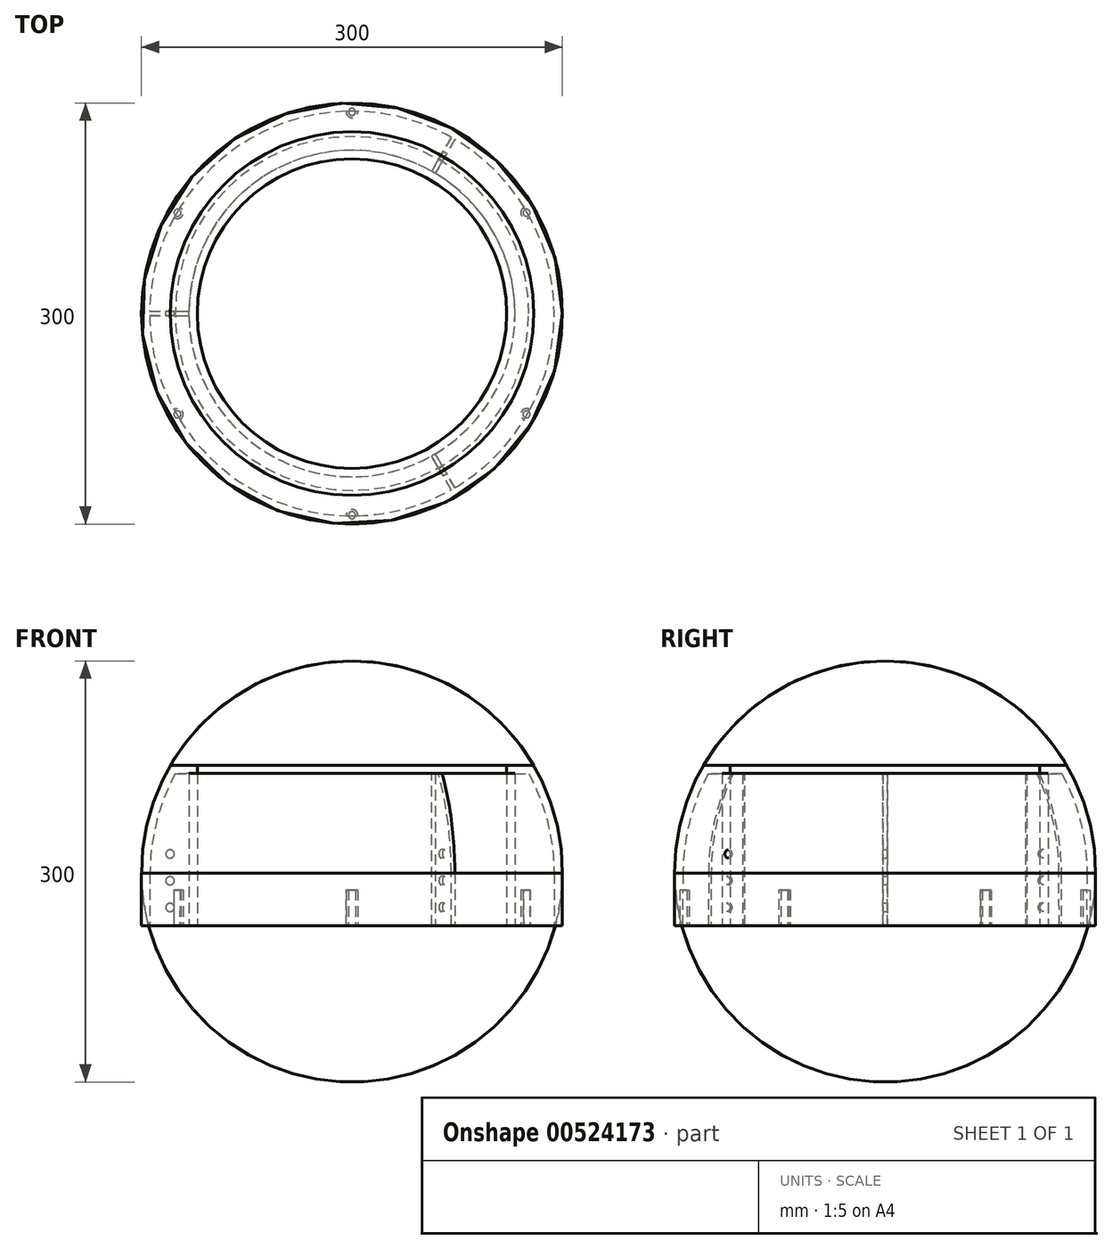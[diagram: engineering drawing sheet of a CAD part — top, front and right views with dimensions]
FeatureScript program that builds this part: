
annotation { "Feature Type Name" : "Feature", "Feature Type Description" : "" }
export const myFeature = defineFeature(function(context is Context, id is Id, definition is map)
    precondition{}
    {
        {
            var Q0;
            Q0=qCreatedBy(makeId("Front.planeOp"),FACE);
            var sketch = newSketch(context, id + "F0", { "sketchPlane" : qUnion([Q0])});
            skArc(sketch, "E0.trimOffspring", {"start": v(-125.97, 71) * mm, "mid": v(-139.35, 36.6) * mm, "end": v(-144, 0) * mm});
            skLineSegment(sketch, "E1", {"start": v(-116.3, 71.03) * mm, "end": v(-116.3, -24.99) * mm});
            skLineSegment(sketch, "E2", {"start": v(-150, 0) * mm, "end": v(-150, -37.33) * mm});
            skLineSegment(sketch, "E3", {"start": v(-150, -37.33) * mm, "end": v(-116.3, -37.33) * mm});
            skLineSegment(sketch, "E4", {"start": v(-116.3, -37.33) * mm, "end": v(-116.3, -24.99) * mm});
            skLineSegment(sketch, "E5", {"start": v(-144, 0) * mm, "end": v(-144.14, -37.33) * mm});
            skArc(sketch, "E6.trimOffspring", {"start": v(-129.51, 76.97) * mm, "mid": v(-144.96, 39.87) * mm, "end": v(-150, 0) * mm});
            skLineSegment(sketch, "E7", {"start": v(-129.51, 76.97) * mm, "end": v(-116.3, 76.97) * mm});
            skLineSegment(sketch, "E8", {"start": v(-116.3, 71.03) * mm, "end": v(-125.97, 71) * mm});
            skLineSegment(sketch, "E9", {"start": v(-125.99, 70.97) * mm, "end": v(-116.3, 70.97) * mm});
            skLineSegment(sketch, "E10", {"start": v(-110.3, 70.97) * mm, "end": v(-110.3, -37.33) * mm});
            skLineSegment(sketch, "E11", {"start": v(-110.3, -37.33) * mm, "end": v(-116.3, -37.33) * mm});
            skLineSegment(sketch, "E12", {"start": v(-116.3, 76.97) * mm, "end": v(-110.3, 76.97) * mm});
            skLineSegment(sketch, "E13", {"start": v(-110.3, 76.97) * mm, "end": v(-110.3, 70.97) * mm});
            skLineSegment(sketch, "E14", {"start": v(0, -70.43) * mm, "end": v(0, 79.54) * mm, "construction": true});
            skSolve(sketch);
        }
        {
            var Q0;
            {var subQ6=sQuery(id+"F0.wireOp",EDGE,"E2");Q0=makeQuery(id+"F0.imprint","IMPRINT",FACE,{"disambiguationData":[TD([[makeQuery(id+"F0.imprint","IMPRINT",EDGE,{"derivedFrom":subQ6}),1.0]])]});}
            var Q1;
            Q1=sQuery(id+"F0.wireOp",EDGE,"E14");
            revolve(context, id + "F1", {"entities" : qUnion([Q0]), "axis" : qUnion([Q1]), "revolveType" : RevolveType.FULL});
        }
        {
            var Q0;
            Q0=makeQuery(id+"F1.opRevolve","SWEPT_FACE",FACE,{"disambiguationData":[OSD([sQuery(id+"F0.wireOp",EDGE,"E3")])]});
            var sketch = newSketch(context, id + "F2", { "sketchPlane" : qUnion([Q0])});
            skCircle(sketch, "E15", {"center": v(0, 143.67) * mm, "radius": 2.5 * mm});
            skCircle(sketch, "E16", {"center": v(0, 143.67) * mm, "radius": 4.13 * mm});
            skCircle(sketch, "E17.1.0", {"center": v(-124.42, 71.83) * mm, "radius": 2.5 * mm});
            skCircle(sketch, "E17.2.0", {"center": v(-124.42, -71.83) * mm, "radius": 2.5 * mm});
            skCircle(sketch, "E17.3.0", {"center": v(0, -143.67) * mm, "radius": 2.5 * mm});
            skCircle(sketch, "E17.4.0", {"center": v(124.42, -71.83) * mm, "radius": 2.5 * mm});
            skCircle(sketch, "E17.5.0", {"center": v(124.42, 71.83) * mm, "radius": 2.5 * mm});
            skPoint(sketch, "E17.center", {"position": v(0, 0) * mm});
            skCircle(sketch, "E18.1.0", {"center": v(-124.42, -71.83) * mm, "radius": 4.13 * mm});
            skCircle(sketch, "E18.2.0", {"center": v(124.42, -71.83) * mm, "radius": 4.13 * mm});
            skCircle(sketch, "E19.1.0", {"center": v(-124.42, 71.83) * mm, "radius": 4.13 * mm});
            skCircle(sketch, "E19.3.0", {"center": v(0, -143.67) * mm, "radius": 4.13 * mm});
            skCircle(sketch, "E19.5.0", {"center": v(124.42, 71.83) * mm, "radius": 4.13 * mm});
            skSolve(sketch);
        }
        {
            var Q0;
            {var subQ0=sQuery(id+"F2.wireOp",EDGE,"E17.4.0");var subQ1=makeQuery(id+"F1.opRevolve","SWEPT_EDGE",EDGE,{"disambiguationData":[OSD([sQuery(id+"F0.wireOp",EDGE,"E3"),sQuery(id+"F0.wireOp",EDGE,"E5")])]});var subQ2=makeQuery(id+"F2.imprint","INTERSECT",VERTEX,{"disambiguationData":[OD(0.0)],"derivedFrom":[subQ1,subQ0]});Q0=makeQuery(id+"F2.imprint","IMPRINT",FACE,{"disambiguationData":[TD([[makeQuery(id+"F2.imprint","IMPRINT",EDGE,{"disambiguationData":[TD([[subQ2,-1.0]])],"derivedFrom":subQ0}),1.0]])]});}
            var Q1;
            {var subQ0=sQuery(id+"F2.wireOp",EDGE,"E15");var subQ1=makeQuery(id+"F1.opRevolve","SWEPT_EDGE",EDGE,{"disambiguationData":[OSD([sQuery(id+"F0.wireOp",EDGE,"E3"),sQuery(id+"F0.wireOp",EDGE,"E5")])]});var subQ2=makeQuery(id+"F2.imprint","INTERSECT",VERTEX,{"disambiguationData":[OD(0.0)],"derivedFrom":[subQ1,subQ0]});Q1=makeQuery(id+"F2.imprint","IMPRINT",FACE,{"disambiguationData":[TD([[makeQuery(id+"F2.imprint","IMPRINT",EDGE,{"disambiguationData":[TD([[subQ2,1.0]])],"derivedFrom":subQ0}),-1.0]])]});}
            var Q2;
            {var subQ0=sQuery(id+"F2.wireOp",EDGE,"E15");var subQ1=makeQuery(id+"F1.opRevolve","SWEPT_EDGE",EDGE,{"disambiguationData":[OSD([sQuery(id+"F0.wireOp",EDGE,"E3"),sQuery(id+"F0.wireOp",EDGE,"E5")])]});var subQ2=makeQuery(id+"F2.imprint","INTERSECT",VERTEX,{"disambiguationData":[OD(0.0)],"derivedFrom":[subQ1,subQ0]});Q2=makeQuery(id+"F2.imprint","IMPRINT",FACE,{"disambiguationData":[TD([[makeQuery(id+"F2.imprint","IMPRINT",EDGE,{"disambiguationData":[TD([[subQ2,-1.0]])],"derivedFrom":subQ0}),-1.0]])]});}
            var Q3;
            {var subQ0=sQuery(id+"F2.wireOp",EDGE,"E17.1.0");var subQ1=makeQuery(id+"F1.opRevolve","SWEPT_EDGE",EDGE,{"disambiguationData":[OSD([sQuery(id+"F0.wireOp",EDGE,"E3"),sQuery(id+"F0.wireOp",EDGE,"E5")])]});var subQ2=makeQuery(id+"F2.imprint","INTERSECT",VERTEX,{"disambiguationData":[OD(0.0)],"derivedFrom":[subQ1,subQ0]});Q3=makeQuery(id+"F2.imprint","IMPRINT",FACE,{"disambiguationData":[TD([[makeQuery(id+"F2.imprint","IMPRINT",EDGE,{"disambiguationData":[TD([[subQ2,-1.0]])],"derivedFrom":subQ0}),-1.0]])]});}
            var Q4;
            {var subQ0=sQuery(id+"F2.wireOp",EDGE,"E17.1.0");var subQ1=makeQuery(id+"F1.opRevolve","SWEPT_EDGE",EDGE,{"disambiguationData":[OSD([sQuery(id+"F0.wireOp",EDGE,"E3"),sQuery(id+"F0.wireOp",EDGE,"E5")])]});var subQ2=makeQuery(id+"F2.imprint","INTERSECT",VERTEX,{"disambiguationData":[OD(0.0)],"derivedFrom":[subQ1,subQ0]});Q4=makeQuery(id+"F2.imprint","IMPRINT",FACE,{"disambiguationData":[TD([[makeQuery(id+"F2.imprint","IMPRINT",EDGE,{"disambiguationData":[TD([[subQ2,1.0]])],"derivedFrom":subQ0}),-1.0]])]});}
            var Q5;
            {var subQ0=sQuery(id+"F2.wireOp",EDGE,"E17.5.0");var subQ1=makeQuery(id+"F1.opRevolve","SWEPT_EDGE",EDGE,{"disambiguationData":[OSD([sQuery(id+"F0.wireOp",EDGE,"E3"),sQuery(id+"F0.wireOp",EDGE,"E5")])]});var subQ2=makeQuery(id+"F2.imprint","INTERSECT",VERTEX,{"disambiguationData":[OD(0.0)],"derivedFrom":[subQ1,subQ0]});Q5=makeQuery(id+"F2.imprint","IMPRINT",FACE,{"disambiguationData":[TD([[makeQuery(id+"F2.imprint","IMPRINT",EDGE,{"disambiguationData":[TD([[subQ2,-1.0]])],"derivedFrom":subQ0}),-1.0]])]});}
            var Q6;
            {var subQ0=sQuery(id+"F2.wireOp",EDGE,"E17.5.0");var subQ1=makeQuery(id+"F1.opRevolve","SWEPT_EDGE",EDGE,{"disambiguationData":[OSD([sQuery(id+"F0.wireOp",EDGE,"E3"),sQuery(id+"F0.wireOp",EDGE,"E5")])]});var subQ2=makeQuery(id+"F2.imprint","INTERSECT",VERTEX,{"disambiguationData":[OD(0.0)],"derivedFrom":[subQ1,subQ0]});Q6=makeQuery(id+"F2.imprint","IMPRINT",FACE,{"disambiguationData":[TD([[makeQuery(id+"F2.imprint","IMPRINT",EDGE,{"disambiguationData":[TD([[subQ2,1.0]])],"derivedFrom":subQ0}),-1.0]])]});}
            var Q7;
            {var subQ0=sQuery(id+"F2.wireOp",EDGE,"E17.2.0");var subQ1=makeQuery(id+"F1.opRevolve","SWEPT_EDGE",EDGE,{"disambiguationData":[OSD([sQuery(id+"F0.wireOp",EDGE,"E3"),sQuery(id+"F0.wireOp",EDGE,"E5")])]});var subQ2=makeQuery(id+"F2.imprint","INTERSECT",VERTEX,{"disambiguationData":[OD(0.0)],"derivedFrom":[subQ1,subQ0]});Q7=makeQuery(id+"F2.imprint","IMPRINT",FACE,{"disambiguationData":[TD([[makeQuery(id+"F2.imprint","IMPRINT",EDGE,{"disambiguationData":[TD([[subQ2,-1.0]])],"derivedFrom":subQ0}),-1.0]])]});}
            var Q8;
            {var subQ0=sQuery(id+"F2.wireOp",EDGE,"E17.2.0");var subQ1=makeQuery(id+"F1.opRevolve","SWEPT_EDGE",EDGE,{"disambiguationData":[OSD([sQuery(id+"F0.wireOp",EDGE,"E3"),sQuery(id+"F0.wireOp",EDGE,"E5")])]});var subQ2=makeQuery(id+"F2.imprint","INTERSECT",VERTEX,{"disambiguationData":[OD(0.0)],"derivedFrom":[subQ1,subQ0]});Q8=makeQuery(id+"F2.imprint","IMPRINT",FACE,{"disambiguationData":[TD([[makeQuery(id+"F2.imprint","IMPRINT",EDGE,{"disambiguationData":[TD([[subQ2,1.0]])],"derivedFrom":subQ0}),-1.0]])]});}
            var Q9;
            {var subQ0=sQuery(id+"F2.wireOp",EDGE,"E17.2.0");var subQ1=makeQuery(id+"F1.opRevolve","SWEPT_EDGE",EDGE,{"disambiguationData":[OSD([sQuery(id+"F0.wireOp",EDGE,"E3"),sQuery(id+"F0.wireOp",EDGE,"E5")])]});var subQ2=makeQuery(id+"F2.imprint","INTERSECT",VERTEX,{"disambiguationData":[OD(0.0)],"derivedFrom":[subQ1,subQ0]});Q9=makeQuery(id+"F2.imprint","IMPRINT",FACE,{"disambiguationData":[TD([[makeQuery(id+"F2.imprint","IMPRINT",EDGE,{"disambiguationData":[TD([[subQ2,-1.0]])],"derivedFrom":subQ0}),1.0]])]});}
            var Q10;
            {var subQ0=sQuery(id+"F2.wireOp",EDGE,"E17.4.0");var subQ1=makeQuery(id+"F1.opRevolve","SWEPT_EDGE",EDGE,{"disambiguationData":[OSD([sQuery(id+"F0.wireOp",EDGE,"E3"),sQuery(id+"F0.wireOp",EDGE,"E5")])]});var subQ2=makeQuery(id+"F2.imprint","INTERSECT",VERTEX,{"disambiguationData":[OD(0.0)],"derivedFrom":[subQ1,subQ0]});Q10=makeQuery(id+"F2.imprint","IMPRINT",FACE,{"disambiguationData":[TD([[makeQuery(id+"F2.imprint","IMPRINT",EDGE,{"disambiguationData":[TD([[subQ2,-1.0]])],"derivedFrom":subQ0}),-1.0]])]});}
            var Q11;
            {var subQ0=sQuery(id+"F2.wireOp",EDGE,"E17.4.0");var subQ1=makeQuery(id+"F1.opRevolve","SWEPT_EDGE",EDGE,{"disambiguationData":[OSD([sQuery(id+"F0.wireOp",EDGE,"E3"),sQuery(id+"F0.wireOp",EDGE,"E5")])]});var subQ2=makeQuery(id+"F2.imprint","INTERSECT",VERTEX,{"disambiguationData":[OD(0.0)],"derivedFrom":[subQ1,subQ0]});Q11=makeQuery(id+"F2.imprint","IMPRINT",FACE,{"disambiguationData":[TD([[makeQuery(id+"F2.imprint","IMPRINT",EDGE,{"disambiguationData":[TD([[subQ2,1.0]])],"derivedFrom":subQ0}),-1.0]])]});}
            var Q12;
            {var subQ0=sQuery(id+"F2.wireOp",EDGE,"E17.3.0");var subQ1=makeQuery(id+"F1.opRevolve","SWEPT_EDGE",EDGE,{"disambiguationData":[OSD([sQuery(id+"F0.wireOp",EDGE,"E3"),sQuery(id+"F0.wireOp",EDGE,"E5")])]});var subQ2=makeQuery(id+"F2.imprint","INTERSECT",VERTEX,{"disambiguationData":[OD(0.0)],"derivedFrom":[subQ1,subQ0]});Q12=makeQuery(id+"F2.imprint","IMPRINT",FACE,{"disambiguationData":[TD([[makeQuery(id+"F2.imprint","IMPRINT",EDGE,{"disambiguationData":[TD([[subQ2,1.0]])],"derivedFrom":subQ0}),-1.0]])]});}
            extrude(context, id + "F3", {"entities" : qUnion([Q0, Q1, Q2, Q3, Q4, Q5, Q6, Q7, Q8, Q9, Q10, Q11, Q12]), "operationType" : NewBodyOperationType.ADD, "oppositeDirection" : true, "depth" : 25.4 * mm});
        }
        {
            var Q0;
            {var subQ0=sQuery(id+"F2.wireOp",EDGE,"E17.1.0");var subQ1=makeQuery(id+"F1.opRevolve","SWEPT_EDGE",EDGE,{"disambiguationData":[OSD([sQuery(id+"F0.wireOp",EDGE,"E3"),sQuery(id+"F0.wireOp",EDGE,"E5")])]});var subQ2=makeQuery(id+"F2.imprint","INTERSECT",VERTEX,{"disambiguationData":[OD(0.0)],"derivedFrom":[subQ1,subQ0]});Q0=makeQuery(id+"F2.imprint","IMPRINT",FACE,{"disambiguationData":[TD([[makeQuery(id+"F2.imprint","IMPRINT",EDGE,{"disambiguationData":[TD([[subQ2,1.0]])],"derivedFrom":subQ0}),1.0]])]});}
            var Q1;
            {var subQ0=sQuery(id+"F2.wireOp",EDGE,"E17.1.0");var subQ1=makeQuery(id+"F1.opRevolve","SWEPT_EDGE",EDGE,{"disambiguationData":[OSD([sQuery(id+"F0.wireOp",EDGE,"E3"),sQuery(id+"F0.wireOp",EDGE,"E5")])]});var subQ2=makeQuery(id+"F2.imprint","INTERSECT",VERTEX,{"disambiguationData":[OD(0.0)],"derivedFrom":[subQ1,subQ0]});Q1=makeQuery(id+"F2.imprint","IMPRINT",FACE,{"disambiguationData":[TD([[makeQuery(id+"F2.imprint","IMPRINT",EDGE,{"disambiguationData":[TD([[subQ2,-1.0]])],"derivedFrom":subQ0}),1.0]])]});}
            var Q2;
            {var subQ0=sQuery(id+"F2.wireOp",EDGE,"E15");var subQ1=makeQuery(id+"F1.opRevolve","SWEPT_EDGE",EDGE,{"disambiguationData":[OSD([sQuery(id+"F0.wireOp",EDGE,"E3"),sQuery(id+"F0.wireOp",EDGE,"E5")])]});var subQ2=makeQuery(id+"F2.imprint","INTERSECT",VERTEX,{"disambiguationData":[OD(0.0)],"derivedFrom":[subQ1,subQ0]});Q2=makeQuery(id+"F2.imprint","IMPRINT",FACE,{"disambiguationData":[TD([[makeQuery(id+"F2.imprint","IMPRINT",EDGE,{"disambiguationData":[TD([[subQ2,1.0]])],"derivedFrom":subQ0}),1.0]])]});}
            var Q3;
            {var subQ0=sQuery(id+"F2.wireOp",EDGE,"E15");var subQ1=makeQuery(id+"F1.opRevolve","SWEPT_EDGE",EDGE,{"disambiguationData":[OSD([sQuery(id+"F0.wireOp",EDGE,"E3"),sQuery(id+"F0.wireOp",EDGE,"E5")])]});var subQ2=makeQuery(id+"F2.imprint","INTERSECT",VERTEX,{"disambiguationData":[OD(0.0)],"derivedFrom":[subQ1,subQ0]});Q3=makeQuery(id+"F2.imprint","IMPRINT",FACE,{"disambiguationData":[TD([[makeQuery(id+"F2.imprint","IMPRINT",EDGE,{"disambiguationData":[TD([[subQ2,-1.0]])],"derivedFrom":subQ0}),1.0]])]});}
            var Q4;
            {var subQ0=sQuery(id+"F2.wireOp",EDGE,"E17.5.0");var subQ1=makeQuery(id+"F1.opRevolve","SWEPT_EDGE",EDGE,{"disambiguationData":[OSD([sQuery(id+"F0.wireOp",EDGE,"E3"),sQuery(id+"F0.wireOp",EDGE,"E5")])]});var subQ2=makeQuery(id+"F2.imprint","INTERSECT",VERTEX,{"disambiguationData":[OD(0.0)],"derivedFrom":[subQ1,subQ0]});Q4=makeQuery(id+"F2.imprint","IMPRINT",FACE,{"disambiguationData":[TD([[makeQuery(id+"F2.imprint","IMPRINT",EDGE,{"disambiguationData":[TD([[subQ2,1.0]])],"derivedFrom":subQ0}),1.0]])]});}
            var Q5;
            {var subQ0=sQuery(id+"F2.wireOp",EDGE,"E17.5.0");var subQ1=makeQuery(id+"F1.opRevolve","SWEPT_EDGE",EDGE,{"disambiguationData":[OSD([sQuery(id+"F0.wireOp",EDGE,"E3"),sQuery(id+"F0.wireOp",EDGE,"E5")])]});var subQ2=makeQuery(id+"F2.imprint","INTERSECT",VERTEX,{"disambiguationData":[OD(0.0)],"derivedFrom":[subQ1,subQ0]});Q5=makeQuery(id+"F2.imprint","IMPRINT",FACE,{"disambiguationData":[TD([[makeQuery(id+"F2.imprint","IMPRINT",EDGE,{"disambiguationData":[TD([[subQ2,-1.0]])],"derivedFrom":subQ0}),1.0]])]});}
            var Q6;
            {var subQ0=sQuery(id+"F2.wireOp",EDGE,"E17.2.0");var subQ1=makeQuery(id+"F1.opRevolve","SWEPT_EDGE",EDGE,{"disambiguationData":[OSD([sQuery(id+"F0.wireOp",EDGE,"E3"),sQuery(id+"F0.wireOp",EDGE,"E5")])]});var subQ2=makeQuery(id+"F2.imprint","INTERSECT",VERTEX,{"disambiguationData":[OD(0.0)],"derivedFrom":[subQ1,subQ0]});Q6=makeQuery(id+"F2.imprint","IMPRINT",FACE,{"disambiguationData":[TD([[makeQuery(id+"F2.imprint","IMPRINT",EDGE,{"disambiguationData":[TD([[subQ2,-1.0]])],"derivedFrom":subQ0}),1.0]])]});}
            var Q7;
            {var subQ0=sQuery(id+"F2.wireOp",EDGE,"E17.2.0");var subQ1=makeQuery(id+"F1.opRevolve","SWEPT_EDGE",EDGE,{"disambiguationData":[OSD([sQuery(id+"F0.wireOp",EDGE,"E3"),sQuery(id+"F0.wireOp",EDGE,"E5")])]});var subQ2=makeQuery(id+"F2.imprint","INTERSECT",VERTEX,{"disambiguationData":[OD(0.0)],"derivedFrom":[subQ1,subQ0]});Q7=makeQuery(id+"F2.imprint","IMPRINT",FACE,{"disambiguationData":[TD([[makeQuery(id+"F2.imprint","IMPRINT",EDGE,{"disambiguationData":[TD([[subQ2,1.0]])],"derivedFrom":subQ0}),1.0]])]});}
            var Q8;
            {var subQ0=sQuery(id+"F2.wireOp",EDGE,"E17.3.0");var subQ1=makeQuery(id+"F1.opRevolve","SWEPT_EDGE",EDGE,{"disambiguationData":[OSD([sQuery(id+"F0.wireOp",EDGE,"E3"),sQuery(id+"F0.wireOp",EDGE,"E5")])]});var subQ2=makeQuery(id+"F2.imprint","INTERSECT",VERTEX,{"disambiguationData":[OD(0.0)],"derivedFrom":[subQ1,subQ0]});Q8=makeQuery(id+"F2.imprint","IMPRINT",FACE,{"disambiguationData":[TD([[makeQuery(id+"F2.imprint","IMPRINT",EDGE,{"disambiguationData":[TD([[subQ2,-1.0]])],"derivedFrom":subQ0}),1.0]])]});}
            var Q9;
            {var subQ0=sQuery(id+"F2.wireOp",EDGE,"E17.3.0");var subQ1=makeQuery(id+"F1.opRevolve","SWEPT_EDGE",EDGE,{"disambiguationData":[OSD([sQuery(id+"F0.wireOp",EDGE,"E3"),sQuery(id+"F0.wireOp",EDGE,"E5")])]});var subQ2=makeQuery(id+"F2.imprint","INTERSECT",VERTEX,{"disambiguationData":[OD(0.0)],"derivedFrom":[subQ1,subQ0]});Q9=makeQuery(id+"F2.imprint","IMPRINT",FACE,{"disambiguationData":[TD([[makeQuery(id+"F2.imprint","IMPRINT",EDGE,{"disambiguationData":[TD([[subQ2,1.0]])],"derivedFrom":subQ0}),1.0]])]});}
            var Q10;
            {var subQ0=sQuery(id+"F2.wireOp",EDGE,"E17.4.0");var subQ1=makeQuery(id+"F1.opRevolve","SWEPT_EDGE",EDGE,{"disambiguationData":[OSD([sQuery(id+"F0.wireOp",EDGE,"E3"),sQuery(id+"F0.wireOp",EDGE,"E5")])]});var subQ2=makeQuery(id+"F2.imprint","INTERSECT",VERTEX,{"disambiguationData":[OD(0.0)],"derivedFrom":[subQ1,subQ0]});Q10=makeQuery(id+"F2.imprint","IMPRINT",FACE,{"disambiguationData":[TD([[makeQuery(id+"F2.imprint","IMPRINT",EDGE,{"disambiguationData":[TD([[subQ2,-1.0]])],"derivedFrom":subQ0}),1.0]])]});}
            var Q11;
            {var subQ0=sQuery(id+"F2.wireOp",EDGE,"E17.4.0");var subQ1=makeQuery(id+"F1.opRevolve","SWEPT_EDGE",EDGE,{"disambiguationData":[OSD([sQuery(id+"F0.wireOp",EDGE,"E3"),sQuery(id+"F0.wireOp",EDGE,"E5")])]});var subQ2=makeQuery(id+"F2.imprint","INTERSECT",VERTEX,{"disambiguationData":[OD(0.0)],"derivedFrom":[subQ1,subQ0]});Q11=makeQuery(id+"F2.imprint","IMPRINT",FACE,{"disambiguationData":[TD([[makeQuery(id+"F2.imprint","IMPRINT",EDGE,{"disambiguationData":[TD([[subQ2,1.0]])],"derivedFrom":subQ0}),1.0]])]});}
            extrude(context, id + "F4", {"entities" : qUnion([Q0, Q1, Q2, Q3, Q4, Q5, Q6, Q7, Q8, Q9, Q10, Q11]), "operationType" : NewBodyOperationType.REMOVE, "oppositeDirection" : true, "depth" : 25.4 * mm});
        }
        {
            var Q0;
            {var subQ0=sQuery(id+"F0.wireOp",EDGE,"E4");Q0=makeQuery(id+"F0.imprint","IMPRINT",FACE,{"disambiguationData":[TD([[makeQuery(id+"F0.imprint","IMPRINT",EDGE,{"derivedFrom":subQ0}),1.0]])]});}
            extrude(context, id + "F5", {"entities" : qUnion([Q0]), "operationType" : NewBodyOperationType.ADD, "endBound" : BoundingType.SYMMETRIC, "depth" : 3 * mm});
        }
        {
            var Q0;
            Q0=makeQuery(id+"F5.opExtrude","CAP_FACE",FACE,{"disambiguationData":[OSD([sQuery(id+"F0.wireOp",EDGE,"E0.trimOffspring"),sQuery(id+"F0.wireOp",EDGE,"E1"),sQuery(id+"F0.wireOp",EDGE,"E3"),sQuery(id+"F0.wireOp",EDGE,"E4"),sQuery(id+"F0.wireOp",EDGE,"E5"),sQuery(id+"F0.wireOp",EDGE,"E9")])],"isStart":true});
            var sketch = newSketch(context, id + "F6", { "sketchPlane" : qUnion([Q0])});
            skCircle(sketch, "E20", {"center": v(129.7, 13.75) * mm, "radius": 3 * mm});
            skCircle(sketch, "E21", {"center": v(129.7, -5.3) * mm, "radius": 3 * mm});
            skCircle(sketch, "E22", {"center": v(129.7, -24.35) * mm, "radius": 3 * mm});
            skSolve(sketch);
        }
        {
            var Q0;
            Q0=qSketchRegion(id+"F6",true);
            extrude(context, id + "F7", {"entities" : qUnion([Q0]), "operationType" : NewBodyOperationType.REMOVE, "oppositeDirection" : true, "depth" : 25.4 * mm});
        }
        {
            var Q0;
            Q0=makeQuery(id+"F1.opRevolve","SWEPT_BODY",BODY,{"disambiguationData":[OSD([sQuery(id+"F0.wireOp",EDGE,"E0.trimOffspring"),sQuery(id+"F0.wireOp",EDGE,"E1"),sQuery(id+"F0.wireOp",EDGE,"E2"),sQuery(id+"F0.wireOp",EDGE,"E3"),sQuery(id+"F0.wireOp",EDGE,"E4"),sQuery(id+"F0.wireOp",EDGE,"E5"),sQuery(id+"F0.wireOp",EDGE,"E6.trimOffspring"),sQuery(id+"F0.wireOp",EDGE,"E7"),sQuery(id+"F0.wireOp",EDGE,"E8"),sQuery(id+"F0.wireOp",EDGE,"E10"),sQuery(id+"F0.wireOp",EDGE,"E11"),sQuery(id+"F0.wireOp",EDGE,"E12"),sQuery(id+"F0.wireOp",EDGE,"E13")])]});
            var Q1;
            Q1=sQuery(id+"F0.wireOp",EDGE,"E14");
            circularPattern(context, id + "F8", {"operationType" : NewBodyOperationType.ADD, "entities" : qUnion([Q0]), "axis" : qUnion([Q1]), "angle" : 360 * degree, "instanceCount" : 3, "equalSpace" : true});
        }
    });
